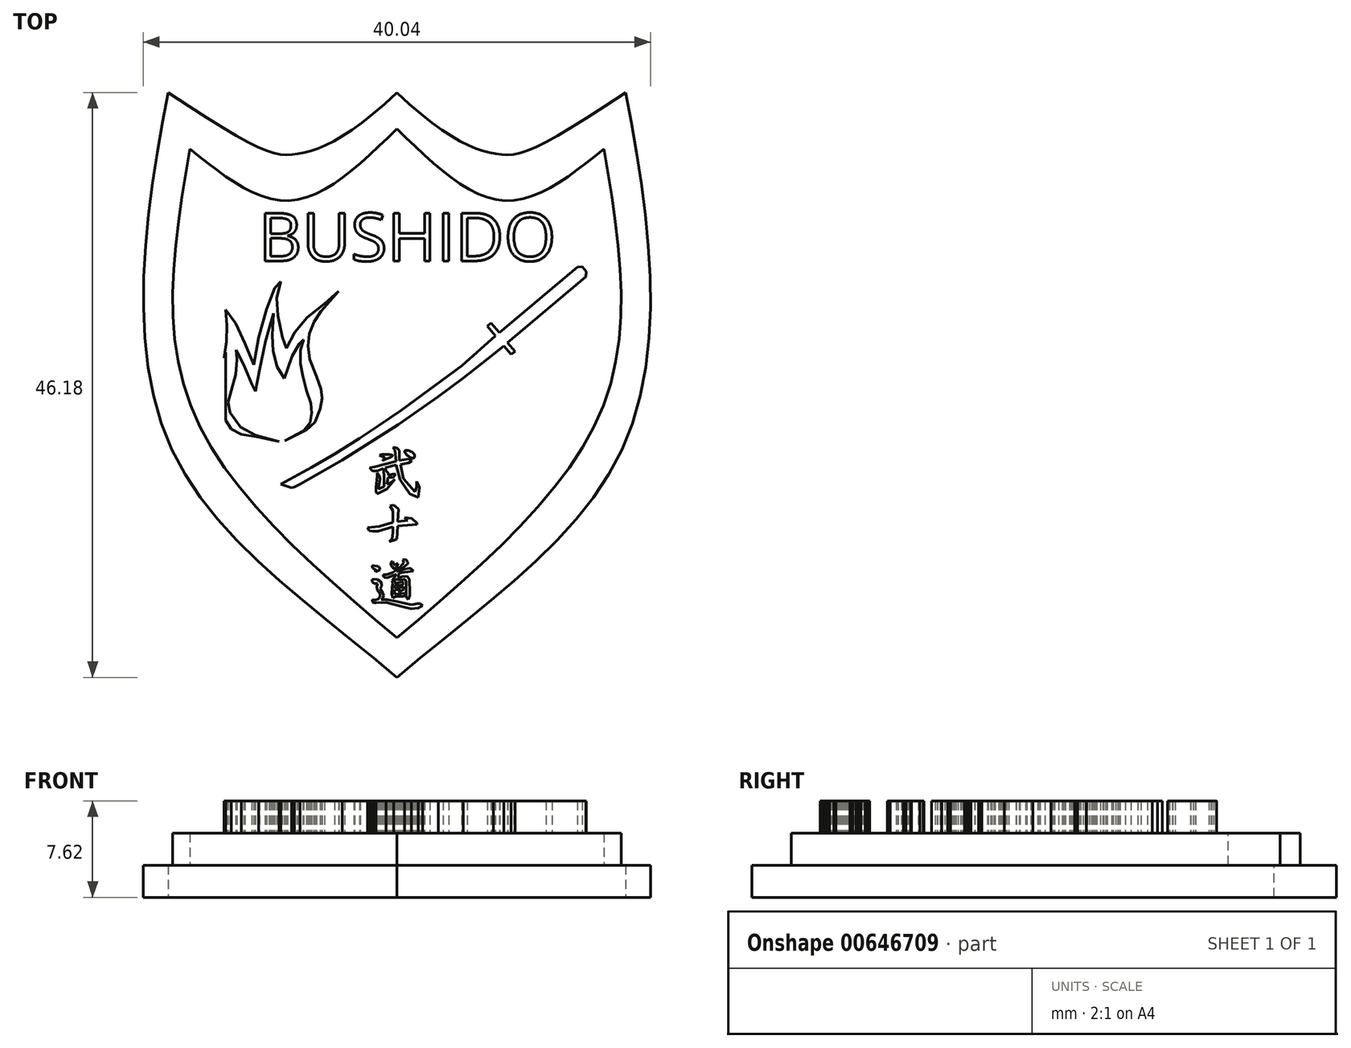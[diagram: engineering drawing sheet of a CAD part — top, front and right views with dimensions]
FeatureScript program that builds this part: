
annotation { "Feature Type Name" : "Feature", "Feature Type Description" : "" }
export const myFeature = defineFeature(function(context is Context, id is Id, definition is map)
    precondition{}
    {
        {
            var Q0;
            Q0=qCreatedBy(makeId("Top.planeOp"),FACE);
            var sketch = newSketch(context, id + "F0", { "sketchPlane" : qUnion([Q0])});
            skFitSpline(sketch, "E0", {"points": [v(0, 0) * mm, v(7.74, -4.83) * mm, v(18.08, 0) * mm], "startDerivative": vector(23.6, -22.28) * mm, "endDerivative": vector(40.6, 26.6) * mm});
            skFitSpline(sketch, "E1", {"points": [v(18.08, 0) * mm, v(18.08, -27.51) * mm, v(0, -46.18) * mm], "startDerivative": vector(10.3, -52.7) * mm, "endDerivative": vector(-42.25, -36.18) * mm});
            skFitSpline(sketch, "E2.MirrorCS", {"points": [v(0, 0) * mm, v(-7.74, -4.83) * mm, v(-18.08, 0) * mm], "startDerivative": vector(-23.6, -22.28) * mm, "endDerivative": vector(-40.6, 26.6) * mm});
            skFitSpline(sketch, "E3.MirrorCS", {"points": [v(-18.08, 0) * mm, v(-18.08, -27.51) * mm, v(0, -46.18) * mm], "startDerivative": vector(-10.3, -52.7) * mm, "endDerivative": vector(42.25, -36.18) * mm});
            skSolve(sketch);
        }
        {
            var Q0;
            Q0=makeQuery(id+"F0.imprint","IMPRINT",FACE,{"disambiguationData":[TD([[makeQuery(id+"F0.imprint","IMPRINT",EDGE,{"derivedFrom":sQuery(id+"F0.wireOp",EDGE,"E0")}),-1.0]])]});
            extrude(context, id + "F1", {"entities" : qUnion([Q0]), "depth" : 2.54 * mm, "offsetDistance" : 25.4 * mm});
        }
        {
            var Q0;
            Q0=qCreatedBy(makeId("Top.planeOp"),FACE);
            var sketch = newSketch(context, id + "F2", { "sketchPlane" : qUnion([Q0])});
            skFitSpline(sketch, "E4", {"points": [v(0, -2.86) * mm, v(8.47, -8.53) * mm, v(16.36, -4.44) * mm], "startDerivative": vector(16.38, -16) * mm, "endDerivative": vector(16.34, 13.17) * mm});
            skFitSpline(sketch, "E5", {"points": [v(16.36, -4.44) * mm, v(16.36, -24.54) * mm, v(0, -43.06) * mm], "startDerivative": vector(7.38, -44.1) * mm, "endDerivative": vector(-39.3, -33.35) * mm});
            skFitSpline(sketch, "E6.MirrorCS", {"points": [v(0, -2.86) * mm, v(-8.47, -8.53) * mm, v(-16.36, -4.44) * mm], "startDerivative": vector(-16.38, -16) * mm, "endDerivative": vector(-16.34, 13.17) * mm});
            skFitSpline(sketch, "E7.MirrorCS", {"points": [v(-16.36, -4.44) * mm, v(-16.36, -24.54) * mm, v(0, -43.06) * mm], "startDerivative": vector(-7.38, -44.1) * mm, "endDerivative": vector(39.3, -33.35) * mm});
            skSolve(sketch);
        }
        {
            var Q0;
            Q0 = qSketchRegion(id + "F2", true);
            extrude(context, id + "F3", {"entities" : qUnion([Q0]), "operationType" : NewBodyOperationType.ADD, "depth" : 5.08 * mm, "offsetDistance" : 25.4 * mm});
        }
        {
            var Q0;
            Q0=makeQuery(id+"F3.opExtrude","CAP_FACE",FACE,{"disambiguationData":[OSD([sQuery(id+"F2.wireOp",EDGE,"E4"),sQuery(id+"F2.wireOp",EDGE,"E5"),sQuery(id+"F2.wireOp",EDGE,"E6.MirrorCS"),sQuery(id+"F2.wireOp",EDGE,"E7.MirrorCS")])],"isStart":false});
            var sketch = newSketch(context, id + "F4", { "sketchPlane" : qUnion([Q0])});
            skText(sketch, "E8", { "text": "BUSHIDO", "fontName": "OpenSans-Regular.ttf"});
            const initialGuessF4  = {"E8": [-0.01092, -0.01329, 1, 0, 0.0038]};
            skSetInitialGuess(sketch, initialGuessF4);
            skSolve(sketch);
        }
        {
            var Q0;
            Q0=makeQuery(id+"F4.imprint","IMPRINT",FACE,{"disambiguationData":[TD([[makeQuery(id+"F4.imprint","IMPRINT",EDGE,{"derivedFrom":sQuery(id+"F4.wireOp",EDGE,"E8.sketch_text.stroke-0")}),1.0]])]});
            var sketch = newSketch(context, id + "F5", { "sketchPlane" : qUnion([Q0])});
            skLineSegment(sketch, "E9", {"start": v(8.08, -18.97) * mm, "end": v(14.27, -13.77) * mm});
            skLineSegment(sketch, "E10", {"start": v(14.27, -13.77) * mm, "end": v(14.65, -13.76) * mm});
            skLineSegment(sketch, "E11", {"start": v(14.65, -13.76) * mm, "end": v(14.97, -14.14) * mm});
            skLineSegment(sketch, "E12", {"start": v(14.97, -14.14) * mm, "end": v(14.92, -14.55) * mm});
            skLineSegment(sketch, "E13", {"start": v(14.92, -14.55) * mm, "end": v(8.74, -19.75) * mm});
            skLineSegment(sketch, "E14", {"start": v(7.14, -18.44) * mm, "end": v(7.43, -18.19) * mm});
            skLineSegment(sketch, "E15", {"start": v(7.43, -18.19) * mm, "end": v(9.32, -20.45) * mm});
            skLineSegment(sketch, "E16", {"start": v(9.32, -20.45) * mm, "end": v(9.02, -20.68) * mm});
            skLineSegment(sketch, "E17", {"start": v(9.02, -20.68) * mm, "end": v(7.14, -18.44) * mm});
            skLineSegment(sketch, "E18", {"start": v(8.53, -19) * mm, "end": v(8.48, -19.24) * mm});
            skLineSegment(sketch, "E19", {"start": v(8.48, -19.24) * mm, "end": v(8.81, -19.3) * mm});
            skLineSegment(sketch, "E20", {"start": v(8.81, -19.3) * mm, "end": v(8.85, -19.08) * mm});
            skLineSegment(sketch, "E21", {"start": v(8.85, -19.08) * mm, "end": v(8.53, -19) * mm});
            skLineSegment(sketch, "E22", {"start": v(8.9, -18.68) * mm, "end": v(8.9, -18.96) * mm});
            skLineSegment(sketch, "E23", {"start": v(8.9, -18.96) * mm, "end": v(9.22, -18.97) * mm});
            skLineSegment(sketch, "E24", {"start": v(9.22, -18.97) * mm, "end": v(9.23, -18.76) * mm});
            skLineSegment(sketch, "E25", {"start": v(9.23, -18.76) * mm, "end": v(8.9, -18.68) * mm});
            skLineSegment(sketch, "E26", {"start": v(9.29, -18.35) * mm, "end": v(9.3, -18.68) * mm});
            skLineSegment(sketch, "E27", {"start": v(9.3, -18.68) * mm, "end": v(9.6, -18.67) * mm});
            skLineSegment(sketch, "E28", {"start": v(9.6, -18.67) * mm, "end": v(9.6, -18.42) * mm});
            skLineSegment(sketch, "E29", {"start": v(9.6, -18.42) * mm, "end": v(9.29, -18.35) * mm});
            skLineSegment(sketch, "E30", {"start": v(9.65, -18.05) * mm, "end": v(9.68, -18.32) * mm});
            skLineSegment(sketch, "E31", {"start": v(9.68, -18.32) * mm, "end": v(9.92, -18.4) * mm});
            skLineSegment(sketch, "E32", {"start": v(9.92, -18.4) * mm, "end": v(9.91, -18.14) * mm});
            skLineSegment(sketch, "E33", {"start": v(9.91, -18.14) * mm, "end": v(9.65, -18.05) * mm});
            skLineSegment(sketch, "E34", {"start": v(10.02, -17.74) * mm, "end": v(10.01, -18) * mm});
            skLineSegment(sketch, "E35", {"start": v(10.01, -18) * mm, "end": v(10.3, -18.09) * mm});
            skLineSegment(sketch, "E36", {"start": v(10.3, -18.09) * mm, "end": v(10.37, -17.86) * mm});
            skLineSegment(sketch, "E37", {"start": v(10.37, -17.86) * mm, "end": v(10.02, -17.74) * mm});
            skLineSegment(sketch, "E38", {"start": v(10.4, -17.43) * mm, "end": v(10.36, -17.7) * mm});
            skLineSegment(sketch, "E39", {"start": v(10.36, -17.7) * mm, "end": v(10.69, -17.73) * mm});
            skLineSegment(sketch, "E40", {"start": v(10.69, -17.73) * mm, "end": v(10.72, -17.52) * mm});
            skLineSegment(sketch, "E41", {"start": v(10.72, -17.52) * mm, "end": v(10.4, -17.43) * mm});
            skLineSegment(sketch, "E42", {"start": v(10.76, -17.12) * mm, "end": v(10.72, -17.36) * mm});
            skLineSegment(sketch, "E43", {"start": v(10.72, -17.36) * mm, "end": v(11.02, -17.4) * mm});
            skLineSegment(sketch, "E44", {"start": v(11.02, -17.4) * mm, "end": v(11.05, -17.22) * mm});
            skLineSegment(sketch, "E45", {"start": v(11.05, -17.22) * mm, "end": v(10.76, -17.12) * mm});
            skLineSegment(sketch, "E46", {"start": v(11.16, -16.79) * mm, "end": v(11.13, -17.06) * mm});
            skLineSegment(sketch, "E47", {"start": v(11.13, -17.06) * mm, "end": v(11.4, -17.08) * mm});
            skLineSegment(sketch, "E48", {"start": v(11.4, -17.08) * mm, "end": v(11.44, -16.9) * mm});
            skLineSegment(sketch, "E49", {"start": v(11.44, -16.9) * mm, "end": v(11.16, -16.79) * mm});
            skLineSegment(sketch, "E50", {"start": v(11.53, -16.45) * mm, "end": v(11.5, -16.7) * mm});
            skLineSegment(sketch, "E51", {"start": v(11.5, -16.7) * mm, "end": v(11.8, -16.76) * mm});
            skLineSegment(sketch, "E52", {"start": v(11.8, -16.76) * mm, "end": v(11.83, -16.54) * mm});
            skLineSegment(sketch, "E53", {"start": v(11.83, -16.54) * mm, "end": v(11.53, -16.45) * mm});
            skLineSegment(sketch, "E54", {"start": v(11.94, -16.13) * mm, "end": v(11.88, -16.4) * mm});
            skLineSegment(sketch, "E55", {"start": v(11.88, -16.4) * mm, "end": v(12.13, -16.46) * mm});
            skLineSegment(sketch, "E56", {"start": v(12.13, -16.46) * mm, "end": v(12.18, -16.24) * mm});
            skLineSegment(sketch, "E57", {"start": v(12.18, -16.24) * mm, "end": v(11.94, -16.13) * mm});
            skLineSegment(sketch, "E58", {"start": v(12.29, -15.84) * mm, "end": v(12.24, -16.12) * mm});
            skLineSegment(sketch, "E59", {"start": v(12.24, -16.12) * mm, "end": v(12.5, -16.23) * mm});
            skLineSegment(sketch, "E60", {"start": v(12.5, -16.23) * mm, "end": v(12.6, -15.97) * mm});
            skLineSegment(sketch, "E61", {"start": v(12.6, -15.97) * mm, "end": v(12.29, -15.84) * mm});
            skLineSegment(sketch, "E62", {"start": v(12.65, -15.53) * mm, "end": v(12.58, -15.82) * mm});
            skLineSegment(sketch, "E63", {"start": v(12.58, -15.82) * mm, "end": v(12.85, -15.88) * mm});
            skLineSegment(sketch, "E64", {"start": v(12.85, -15.88) * mm, "end": v(12.9, -15.63) * mm});
            skLineSegment(sketch, "E65", {"start": v(12.9, -15.63) * mm, "end": v(12.65, -15.53) * mm});
            skLineSegment(sketch, "E66", {"start": v(13.04, -15.2) * mm, "end": v(12.99, -15.5) * mm});
            skLineSegment(sketch, "E67", {"start": v(12.99, -15.5) * mm, "end": v(13.28, -15.55) * mm});
            skLineSegment(sketch, "E68", {"start": v(13.28, -15.55) * mm, "end": v(13.33, -15.3) * mm});
            skLineSegment(sketch, "E69", {"start": v(13.33, -15.3) * mm, "end": v(13.04, -15.2) * mm});
            skLineSegment(sketch, "E70", {"start": v(13.43, -14.88) * mm, "end": v(13.33, -15.13) * mm});
            skLineSegment(sketch, "E71", {"start": v(13.33, -15.13) * mm, "end": v(13.6, -15.23) * mm});
            skLineSegment(sketch, "E72", {"start": v(13.6, -15.23) * mm, "end": v(13.68, -15.02) * mm});
            skLineSegment(sketch, "E73", {"start": v(13.68, -15.02) * mm, "end": v(13.43, -14.88) * mm});
            skLineSegment(sketch, "E74", {"start": v(13.79, -14.58) * mm, "end": v(13.7, -14.83) * mm});
            skLineSegment(sketch, "E75", {"start": v(13.7, -14.83) * mm, "end": v(13.96, -14.94) * mm});
            skLineSegment(sketch, "E76", {"start": v(13.96, -14.94) * mm, "end": v(14.05, -14.71) * mm});
            skLineSegment(sketch, "E77", {"start": v(14.05, -14.71) * mm, "end": v(13.79, -14.58) * mm});
            skPoint(sketch, "E78.orphan", {"position": v(13.8, -14.57) * mm});
            skLineSegment(sketch, "E79", {"start": v(14.13, -14.25) * mm, "end": v(14.09, -14.5) * mm});
            skPoint(sketch, "E79.endSnap0", {"position": v(13.55, -14.95) * mm});
            skLineSegment(sketch, "E80", {"start": v(14.09, -14.5) * mm, "end": v(14.38, -14.64) * mm});
            skLineSegment(sketch, "E81", {"start": v(14.38, -14.64) * mm, "end": v(14.43, -14.35) * mm});
            skLineSegment(sketch, "E82", {"start": v(14.43, -14.35) * mm, "end": v(14.13, -14.25) * mm});
            skLineSegment(sketch, "E83", {"start": v(7.79, -19.21) * mm, "end": v(7.5, -19.97) * mm});
            skLineSegment(sketch, "E84", {"start": v(7.5, -19.97) * mm, "end": v(8.44, -20) * mm});
            skLineSegment(sketch, "E85", {"start": v(8.44, -20) * mm, "end": v(7.62, -20.68) * mm});
            skLineSegment(sketch, "E86", {"start": v(7.62, -20.68) * mm, "end": v(5.23, -22.54) * mm});
            skLineSegment(sketch, "E87", {"start": v(5.23, -22.54) * mm, "end": v(3.27, -23.99) * mm});
            skLineSegment(sketch, "E88", {"start": v(3.27, -23.99) * mm, "end": v(0.1, -26.23) * mm});
            skLineSegment(sketch, "E89", {"start": v(0.1, -26.23) * mm, "end": v(-4.31, -29.03) * mm});
            skLineSegment(sketch, "E90", {"start": v(-4.31, -29.03) * mm, "end": v(-7.65, -30.91) * mm});
            skLineSegment(sketch, "E91", {"start": v(-7.65, -30.91) * mm, "end": v(-8.09, -31.14) * mm});
            skLineSegment(sketch, "E92", {"start": v(-8.09, -31.14) * mm, "end": v(-8.32, -31.2) * mm});
            skLineSegment(sketch, "E93", {"start": v(-8.32, -31.2) * mm, "end": v(-9.18, -30.92) * mm});
            skLineSegment(sketch, "E94", {"start": v(-9.18, -30.92) * mm, "end": v(-6.72, -29.6) * mm});
            skLineSegment(sketch, "E95", {"start": v(-6.72, -29.6) * mm, "end": v(-4.93, -28.55) * mm});
            skLineSegment(sketch, "E96", {"start": v(-4.93, -28.55) * mm, "end": v(-2.96, -27.3) * mm});
            skLineSegment(sketch, "E97", {"start": v(-2.96, -27.3) * mm, "end": v(-1.43, -26.28) * mm});
            skLineSegment(sketch, "E98", {"start": v(-1.43, -26.28) * mm, "end": v(0.36, -25.07) * mm});
            skLineSegment(sketch, "E99", {"start": v(0.36, -25.07) * mm, "end": v(1.86, -23.96) * mm});
            skLineSegment(sketch, "E100", {"start": v(1.86, -23.96) * mm, "end": v(3.69, -22.61) * mm});
            skLineSegment(sketch, "E101", {"start": v(3.69, -22.61) * mm, "end": v(5.14, -21.54) * mm});
            skLineSegment(sketch, "E102", {"start": v(5.14, -21.54) * mm, "end": v(7.79, -19.21) * mm});
            skLineSegment(sketch, "E103", {"start": v(7.5, -19.97) * mm, "end": v(5.5, -21.5) * mm});
            skLineSegment(sketch, "E104", {"start": v(5.5, -21.5) * mm, "end": v(3, -23.43) * mm});
            skLineSegment(sketch, "E105", {"start": v(3, -23.43) * mm, "end": v(1.93, -24.22) * mm});
            skLineSegment(sketch, "E106", {"start": v(1.93, -24.22) * mm, "end": v(0.64, -25.17) * mm});
            skLineSegment(sketch, "E107", {"start": v(0.64, -25.17) * mm, "end": v(-0.46, -25.9) * mm});
            skLineSegment(sketch, "E108", {"start": v(-0.46, -25.9) * mm, "end": v(-1.61, -26.68) * mm});
            skLineSegment(sketch, "E109", {"start": v(-1.61, -26.68) * mm, "end": v(-3.6, -28) * mm});
            skLineSegment(sketch, "E110", {"start": v(-3.6, -28) * mm, "end": v(-5.08, -28.93) * mm});
            skLineSegment(sketch, "E111", {"start": v(-5.08, -28.93) * mm, "end": v(-6.93, -30) * mm});
            skLineSegment(sketch, "E112", {"start": v(-6.93, -30) * mm, "end": v(-8.23, -30.68) * mm});
            skLineSegment(sketch, "E113", {"start": v(-8.23, -30.68) * mm, "end": v(-9.18, -30.92) * mm});
            skLineSegment(sketch, "E114.0", {"start": v(7.79, -19.21) * mm, "end": v(8.08, -18.97) * mm, "construction": true});
            skLineSegment(sketch, "E115.0", {"start": v(8.53, -19) * mm, "end": v(13.8, -14.57) * mm, "construction": true});
            skLineSegment(sketch, "E116.0", {"start": v(13.55, -14.95) * mm, "end": v(14.09, -14.5) * mm, "construction": true});
            skLineSegment(sketch, "E117.0", {"start": v(8.44, -20) * mm, "end": v(8.74, -19.75) * mm, "construction": true});
            skLineSegment(sketch, "E118.0", {"start": v(5.5, -21.5) * mm, "end": v(14.13, -14.25) * mm, "construction": true});
            skLineSegment(sketch, "E119.0", {"start": v(-0.46, -25.9) * mm, "end": v(1.86, -23.96) * mm, "construction": true});
            skLineSegment(sketch, "E120.0", {"start": v(8.08, -18.97) * mm, "end": v(7.43, -18.19) * mm, "construction": true});
            skLineSegment(sketch, "E121.0", {"start": v(9.02, -20.68) * mm, "end": v(7.14, -18.44) * mm, "construction": true});
            skSolve(sketch);
        }
        {
            var Q0;
            Q0=makeQuery(id+"F4.imprint","IMPRINT",FACE,{"disambiguationData":[TD([[makeQuery(id+"F4.imprint","IMPRINT",EDGE,{"derivedFrom":sQuery(id+"F4.wireOp",EDGE,"E8.sketch_text.stroke-0")}),1.0]])]});
            var sketch = newSketch(context, id + "F6", { "sketchPlane" : qUnion([Q0])});
            skFitSpline(sketch, "E122", {"points": [v(-1.36, -28.64) * mm, v(-0.34, -28.66) * mm, v(-1.13, -29.02) * mm, v(-0.95, -28.87) * mm, v(-1.36, -28.64) * mm]});
            skFitSpline(sketch, "E123", {"points": [v(0.6, -28.32) * mm, v(1.28, -28.87) * mm, v(1.3, -28.46) * mm, v(0.6, -28.32) * mm]});
            skLineSegment(sketch, "E124", {"start": v(-0.32, -27.99) * mm, "end": v(0, -28.06) * mm});
            skLineSegment(sketch, "E125", {"start": v(0, -28.06) * mm, "end": v(0.2, -28.26) * mm});
            skLineSegment(sketch, "E126", {"start": v(0.2, -28.26) * mm, "end": v(0.2, -29.06) * mm});
            skLineSegment(sketch, "E127", {"start": v(0.2, -29.06) * mm, "end": v(0.97, -28.92) * mm});
            skLineSegment(sketch, "E128", {"start": v(0.97, -28.92) * mm, "end": v(1.19, -29.1) * mm});
            skLineSegment(sketch, "E129", {"start": v(1.19, -29.1) * mm, "end": v(0.91, -29.24) * mm});
            skLineSegment(sketch, "E130", {"start": v(0.91, -29.24) * mm, "end": v(0.3, -29.36) * mm});
            skLineSegment(sketch, "E131", {"start": v(0.3, -29.36) * mm, "end": v(0.5, -30.49) * mm});
            skLineSegment(sketch, "E132", {"start": v(0.5, -30.49) * mm, "end": v(1.42, -31.54) * mm});
            skLineSegment(sketch, "E133", {"start": v(1.42, -31.54) * mm, "end": v(1.57, -31.13) * mm});
            skLineSegment(sketch, "E134", {"start": v(1.57, -31.13) * mm, "end": v(1.57, -30.7) * mm});
            skLineSegment(sketch, "E135", {"start": v(1.57, -30.7) * mm, "end": v(1.79, -31.19) * mm});
            skLineSegment(sketch, "E136", {"start": v(1.79, -31.19) * mm, "end": v(1.7, -31.96) * mm});
            skLineSegment(sketch, "E137", {"start": v(1.7, -31.96) * mm, "end": v(1.01, -31.69) * mm});
            skLineSegment(sketch, "E138", {"start": v(1.01, -31.69) * mm, "end": v(0.24, -30.58) * mm});
            skLineSegment(sketch, "E139", {"start": v(0.24, -30.58) * mm, "end": v(-0.05, -29.4) * mm});
            skLineSegment(sketch, "E140", {"start": v(-0.05, -29.4) * mm, "end": v(-0.92, -29.62) * mm});
            skLineSegment(sketch, "E141", {"start": v(-0.92, -29.62) * mm, "end": v(-0.85, -29.88) * mm});
            skLineSegment(sketch, "E142", {"start": v(-0.85, -29.88) * mm, "end": v(-0.68, -30.05) * mm});
            skLineSegment(sketch, "E143", {"start": v(-0.68, -30.05) * mm, "end": v(-0.68, -30.21) * mm});
            skLineSegment(sketch, "E144", {"start": v(-0.68, -30.21) * mm, "end": v(-0.36, -30.12) * mm});
            skLineSegment(sketch, "E145", {"start": v(-0.36, -30.12) * mm, "end": v(-0.11, -30.12) * mm});
            skLineSegment(sketch, "E146", {"start": v(-0.11, -30.12) * mm, "end": v(-0.28, -30.4) * mm});
            skLineSegment(sketch, "E147", {"start": v(-0.28, -30.4) * mm, "end": v(-0.7, -30.4) * mm});
            skLineSegment(sketch, "E148", {"start": v(-0.7, -30.4) * mm, "end": v(-0.8, -30.93) * mm});
            skLineSegment(sketch, "E149", {"start": v(-0.8, -30.93) * mm, "end": v(-0.43, -30.76) * mm});
            skLineSegment(sketch, "E150", {"start": v(-0.43, -30.76) * mm, "end": v(-0.16, -30.53) * mm});
            skLineSegment(sketch, "E151", {"start": v(-0.16, -30.53) * mm, "end": v(-0.8, -31.32) * mm});
            skLineSegment(sketch, "E152", {"start": v(-0.8, -31.32) * mm, "end": v(-1.55, -31.69) * mm});
            skLineSegment(sketch, "E153", {"start": v(-1.55, -31.69) * mm, "end": v(-1.65, -31.5) * mm});
            skLineSegment(sketch, "E154", {"start": v(-1.65, -31.5) * mm, "end": v(-1.65, -31.17) * mm});
            skLineSegment(sketch, "E155", {"start": v(-1.65, -31.17) * mm, "end": v(-1.57, -30.28) * mm});
            skLineSegment(sketch, "E156", {"start": v(-1.57, -30.28) * mm, "end": v(-1.57, -30.03) * mm});
            skLineSegment(sketch, "E157", {"start": v(-1.57, -30.03) * mm, "end": v(-1.38, -30.24) * mm});
            skLineSegment(sketch, "E158", {"start": v(-1.38, -30.24) * mm, "end": v(-1.32, -30.5) * mm});
            skLineSegment(sketch, "E159", {"start": v(-1.32, -30.5) * mm, "end": v(-1.46, -31.3) * mm});
            skLineSegment(sketch, "E160", {"start": v(-1.46, -31.3) * mm, "end": v(-1, -31.11) * mm});
            skLineSegment(sketch, "E161", {"start": v(-1, -31.11) * mm, "end": v(-1, -30.23) * mm});
            skLineSegment(sketch, "E162", {"start": v(-1, -30.23) * mm, "end": v(-1.08, -29.68) * mm});
            skLineSegment(sketch, "E163", {"start": v(-1.08, -29.68) * mm, "end": v(-1.57, -29.88) * mm});
            skLineSegment(sketch, "E164", {"start": v(-1.57, -29.88) * mm, "end": v(-1.92, -29.88) * mm});
            skLineSegment(sketch, "E165", {"start": v(-1.92, -29.88) * mm, "end": v(-2.14, -29.63) * mm});
            skLineSegment(sketch, "E166", {"start": v(-2.14, -29.63) * mm, "end": v(-1.79, -29.55) * mm});
            skLineSegment(sketch, "E167", {"start": v(-1.79, -29.55) * mm, "end": v(-0.06, -29.1) * mm});
            skLineSegment(sketch, "E168", {"start": v(-0.06, -29.1) * mm, "end": v(-0.16, -28.24) * mm});
            skLineSegment(sketch, "E169", {"start": v(-0.16, -28.24) * mm, "end": v(-0.32, -27.99) * mm});
            skLineSegment(sketch, "E170", {"start": v(-0.53, -32.65) * mm, "end": v(-0.32, -32.58) * mm});
            skLineSegment(sketch, "E171", {"start": v(-0.32, -32.58) * mm, "end": v(-0.16, -32.65) * mm});
            skLineSegment(sketch, "E172", {"start": v(-0.16, -32.65) * mm, "end": v(0.13, -32.9) * mm});
            skLineSegment(sketch, "E173", {"start": v(0.13, -32.9) * mm, "end": v(0.06, -33.9) * mm});
            skLineSegment(sketch, "E174", {"start": v(0.06, -33.9) * mm, "end": v(0.86, -33.78) * mm});
            skLineSegment(sketch, "E175", {"start": v(0.86, -33.78) * mm, "end": v(0.77, -33.74) * mm});
            skLineSegment(sketch, "E176", {"start": v(0.77, -33.74) * mm, "end": v(0.6, -33.55) * mm});
            skLineSegment(sketch, "E177", {"start": v(0.6, -33.55) * mm, "end": v(1.17, -33.62) * mm});
            skLineSegment(sketch, "E178", {"start": v(1.17, -33.62) * mm, "end": v(1.6, -34) * mm});
            skLineSegment(sketch, "E179", {"start": v(1.6, -34) * mm, "end": v(1.6, -34.11) * mm});
            skLineSegment(sketch, "E180", {"start": v(1.6, -34.11) * mm, "end": v(0.07, -34.21) * mm});
            skLineSegment(sketch, "E181", {"start": v(0.07, -34.21) * mm, "end": v(0, -35.23) * mm});
            skLineSegment(sketch, "E182", {"start": v(0, -35.23) * mm, "end": v(-0.2, -35.34) * mm});
            skLineSegment(sketch, "E183", {"start": v(-0.2, -35.34) * mm, "end": v(-0.6, -35.46) * mm});
            skLineSegment(sketch, "E184", {"start": v(-0.6, -35.46) * mm, "end": v(-0.4, -35.24) * mm});
            skLineSegment(sketch, "E185", {"start": v(-0.4, -35.24) * mm, "end": v(-0.33, -34.77) * mm});
            skLineSegment(sketch, "E186", {"start": v(-0.33, -34.77) * mm, "end": v(-0.33, -34.28) * mm});
            skLineSegment(sketch, "E187", {"start": v(-0.33, -34.28) * mm, "end": v(-1.5, -34.65) * mm});
            skLineSegment(sketch, "E188", {"start": v(-1.5, -34.65) * mm, "end": v(-1.91, -34.65) * mm});
            skLineSegment(sketch, "E189", {"start": v(-1.91, -34.65) * mm, "end": v(-2.2, -34.61) * mm});
            skLineSegment(sketch, "E190", {"start": v(-2.2, -34.61) * mm, "end": v(-2.32, -34.37) * mm});
            skLineSegment(sketch, "E191", {"start": v(-2.32, -34.37) * mm, "end": v(-1.4, -34.27) * mm});
            skLineSegment(sketch, "E192", {"start": v(-1.4, -34.27) * mm, "end": v(-0.32, -33.94) * mm});
            skLineSegment(sketch, "E193", {"start": v(-0.32, -33.94) * mm, "end": v(-0.32, -33) * mm});
            skLineSegment(sketch, "E194", {"start": v(-0.32, -33) * mm, "end": v(-0.53, -32.65) * mm});
            skLineSegment(sketch, "E195", {"start": v(-1.45, -35.63) * mm, "end": v(-0.37, -35.5) * mm});
            skLineSegment(sketch, "E196", {"start": v(-0.37, -35.5) * mm, "end": v(0.26, -35.4) * mm});
            skLineSegment(sketch, "E197", {"start": v(0.26, -35.4) * mm, "end": v(0.53, -35.33) * mm});
            skLineSegment(sketch, "E198", {"start": v(0.53, -35.33) * mm, "end": v(0.72, -35.34) * mm});
            skLineSegment(sketch, "E199", {"start": v(0.72, -35.34) * mm, "end": v(0.95, -35.44) * mm});
            skLineSegment(sketch, "E200", {"start": v(0.95, -35.44) * mm, "end": v(1.05, -35.68) * mm});
            skLineSegment(sketch, "E201", {"start": v(1.05, -35.68) * mm, "end": v(0.77, -35.68) * mm});
            skLineSegment(sketch, "E202", {"start": v(0.77, -35.68) * mm, "end": v(0.35, -35.68) * mm});
            skLineSegment(sketch, "E203", {"start": v(0.35, -35.68) * mm, "end": v(-0.09, -35.68) * mm});
            skLineSegment(sketch, "E204", {"start": v(-0.09, -35.68) * mm, "end": v(-0.72, -35.83) * mm});
            skLineSegment(sketch, "E205", {"start": v(-0.72, -35.83) * mm, "end": v(-1.12, -35.9) * mm});
            skLineSegment(sketch, "E206", {"start": v(-1.12, -35.9) * mm, "end": v(-1.27, -35.83) * mm});
            skLineSegment(sketch, "E207", {"start": v(-1.27, -35.83) * mm, "end": v(-1.45, -35.64) * mm});
            skLineSegment(sketch, "E208", {"start": v(-1.95, -37.35) * mm, "end": v(-1.55, -37.4) * mm});
            skLineSegment(sketch, "E209", {"start": v(-1.55, -37.4) * mm, "end": v(-1.39, -37.48) * mm});
            skLineSegment(sketch, "E210", {"start": v(-1.39, -37.48) * mm, "end": v(-1.34, -37.69) * mm});
            skLineSegment(sketch, "E211", {"start": v(-1.34, -37.69) * mm, "end": v(-1.7, -37.83) * mm});
            skLineSegment(sketch, "E212", {"start": v(-1.7, -37.83) * mm, "end": v(-1.71, -37.73) * mm});
            skLineSegment(sketch, "E213", {"start": v(-1.71, -37.73) * mm, "end": v(-1.63, -37.71) * mm});
            skLineSegment(sketch, "E214", {"start": v(-1.63, -37.71) * mm, "end": v(-1.91, -37.55) * mm});
            skLineSegment(sketch, "E215", {"start": v(-1.91, -37.55) * mm, "end": v(-1.95, -37.35) * mm});
            skLineSegment(sketch, "E216", {"start": v(-0.32, -37.03) * mm, "end": v(-0.3, -37.15) * mm});
            skLineSegment(sketch, "E217", {"start": v(-0.3, -37.15) * mm, "end": v(-0.16, -37.32) * mm});
            skLineSegment(sketch, "E218", {"start": v(-0.16, -37.32) * mm, "end": v(0.1, -37.16) * mm});
            skLineSegment(sketch, "E219", {"start": v(0.1, -37.16) * mm, "end": v(-0.1, -37.67) * mm});
            skLineSegment(sketch, "E220", {"start": v(-0.1, -37.67) * mm, "end": v(-0.36, -37.5) * mm});
            skLineSegment(sketch, "E221", {"start": v(-0.36, -37.5) * mm, "end": v(-0.47, -37.29) * mm});
            skLineSegment(sketch, "E222", {"start": v(-0.47, -37.29) * mm, "end": v(-0.47, -37.11) * mm});
            skLineSegment(sketch, "E223", {"start": v(-0.47, -37.11) * mm, "end": v(-0.32, -37.03) * mm});
            skLineSegment(sketch, "E224", {"start": v(0.5, -36.87) * mm, "end": v(0.71, -36.9) * mm});
            skLineSegment(sketch, "E225", {"start": v(0.71, -36.9) * mm, "end": v(0.84, -37.1) * mm});
            skLineSegment(sketch, "E226", {"start": v(0.84, -37.1) * mm, "end": v(0.87, -37.21) * mm});
            skLineSegment(sketch, "E227", {"start": v(0.87, -37.21) * mm, "end": v(0.39, -37.59) * mm});
            skLineSegment(sketch, "E228", {"start": v(0.39, -37.59) * mm, "end": v(-0.02, -37.77) * mm});
            skLineSegment(sketch, "E229", {"start": v(-0.02, -37.77) * mm, "end": v(0.16, -37.79) * mm});
            skLineSegment(sketch, "E230", {"start": v(0.16, -37.79) * mm, "end": v(0.65, -37.62) * mm});
            skLineSegment(sketch, "E231", {"start": v(0.65, -37.62) * mm, "end": v(1.01, -37.57) * mm});
            skLineSegment(sketch, "E232", {"start": v(1.01, -37.57) * mm, "end": v(1.15, -37.63) * mm});
            skLineSegment(sketch, "E233", {"start": v(1.15, -37.63) * mm, "end": v(1.31, -37.79) * mm});
            skLineSegment(sketch, "E234", {"start": v(1.31, -37.79) * mm, "end": v(0.16, -37.95) * mm});
            skLineSegment(sketch, "E235", {"start": v(0.16, -37.95) * mm, "end": v(0.13, -38.26) * mm});
            skLineSegment(sketch, "E236", {"start": v(0.13, -38.26) * mm, "end": v(0.09, -38.33) * mm});
            skLineSegment(sketch, "E237", {"start": v(0.09, -38.33) * mm, "end": v(0.41, -38.23) * mm});
            skLineSegment(sketch, "E238", {"start": v(0.41, -38.23) * mm, "end": v(0.78, -38.18) * mm});
            skLineSegment(sketch, "E239", {"start": v(0.78, -38.18) * mm, "end": v(1, -38.4) * mm});
            skLineSegment(sketch, "E240", {"start": v(1, -38.4) * mm, "end": v(1.03, -39.54) * mm});
            skLineSegment(sketch, "E241", {"start": v(1.03, -39.54) * mm, "end": v(1, -39.7) * mm});
            skLineSegment(sketch, "E242", {"start": v(1, -39.7) * mm, "end": v(0.88, -40.03) * mm});
            skLineSegment(sketch, "E243", {"start": v(0.88, -40.03) * mm, "end": v(0.71, -39.83) * mm});
            skLineSegment(sketch, "E244", {"start": v(0.71, -39.83) * mm, "end": v(0.71, -38.88) * mm});
            skLineSegment(sketch, "E245", {"start": v(0.71, -38.88) * mm, "end": v(0.71, -38.64) * mm});
            skLineSegment(sketch, "E246", {"start": v(0.71, -38.64) * mm, "end": v(0.64, -38.42) * mm});
            skLineSegment(sketch, "E247", {"start": v(0.64, -38.42) * mm, "end": v(0.42, -38.48) * mm});
            skLineSegment(sketch, "E248", {"start": v(0.42, -38.48) * mm, "end": v(0.11, -38.44) * mm});
            skLineSegment(sketch, "E249", {"start": v(0.11, -38.44) * mm, "end": v(-0.08, -38.44) * mm});
            skLineSegment(sketch, "E250", {"start": v(-0.08, -38.44) * mm, "end": v(-0.2, -38.52) * mm});
            skLineSegment(sketch, "E251", {"start": v(-0.2, -38.52) * mm, "end": v(-0.15, -38.7) * mm});
            skLineSegment(sketch, "E252", {"start": v(-0.15, -38.7) * mm, "end": v(-0.14, -38.74) * mm});
            skLineSegment(sketch, "E253", {"start": v(-0.14, -38.74) * mm, "end": v(0.12, -38.7) * mm});
            skLineSegment(sketch, "E254", {"start": v(0.12, -38.7) * mm, "end": v(0.33, -38.65) * mm});
            skLineSegment(sketch, "E255", {"start": v(0.33, -38.65) * mm, "end": v(0.46, -38.66) * mm});
            skLineSegment(sketch, "E256", {"start": v(0.46, -38.66) * mm, "end": v(0.54, -38.74) * mm});
            skLineSegment(sketch, "E257", {"start": v(0.54, -38.74) * mm, "end": v(0.44, -38.85) * mm});
            skLineSegment(sketch, "E258", {"start": v(0.44, -38.85) * mm, "end": v(0.19, -38.93) * mm});
            skLineSegment(sketch, "E259", {"start": v(0.19, -38.93) * mm, "end": v(0.06, -39.02) * mm});
            skLineSegment(sketch, "E260", {"start": v(0.06, -39.02) * mm, "end": v(0.03, -39) * mm});
            skLineSegment(sketch, "E261", {"start": v(0.03, -39) * mm, "end": v(0.12, -38.92) * mm});
            skLineSegment(sketch, "E262", {"start": v(0.12, -38.92) * mm, "end": v(0.07, -38.9) * mm});
            skLineSegment(sketch, "E263", {"start": v(0.07, -38.9) * mm, "end": v(-0.17, -38.9) * mm});
            skLineSegment(sketch, "E264", {"start": v(-0.17, -38.9) * mm, "end": v(-0.17, -39.14) * mm});
            skLineSegment(sketch, "E265", {"start": v(-0.17, -39.14) * mm, "end": v(0.03, -39.13) * mm});
            skLineSegment(sketch, "E266", {"start": v(0.03, -39.13) * mm, "end": v(0.34, -39.06) * mm});
            skLineSegment(sketch, "E267", {"start": v(0.34, -39.06) * mm, "end": v(0.5, -39.06) * mm});
            skLineSegment(sketch, "E268", {"start": v(0.5, -39.06) * mm, "end": v(0.6, -39.13) * mm});
            skLineSegment(sketch, "E269", {"start": v(0.6, -39.13) * mm, "end": v(0.55, -39.23) * mm});
            skLineSegment(sketch, "E270", {"start": v(0.55, -39.23) * mm, "end": v(0.31, -39.35) * mm});
            skLineSegment(sketch, "E271", {"start": v(0.31, -39.35) * mm, "end": v(0.15, -39.46) * mm});
            skLineSegment(sketch, "E272", {"start": v(0.15, -39.46) * mm, "end": v(0.13, -39.44) * mm});
            skLineSegment(sketch, "E273", {"start": v(0.13, -39.44) * mm, "end": v(0.27, -39.3) * mm});
            skLineSegment(sketch, "E274", {"start": v(0.27, -39.3) * mm, "end": v(-0.15, -39.26) * mm});
            skLineSegment(sketch, "E275", {"start": v(-0.15, -39.26) * mm, "end": v(-0.18, -39.34) * mm});
            skLineSegment(sketch, "E276", {"start": v(-0.18, -39.34) * mm, "end": v(-0.2, -39.62) * mm});
            skLineSegment(sketch, "E277", {"start": v(-0.2, -39.62) * mm, "end": v(-0.06, -39.56) * mm});
            skLineSegment(sketch, "E278", {"start": v(-0.06, -39.56) * mm, "end": v(-0.07, -39.6) * mm});
            skLineSegment(sketch, "E279", {"start": v(-0.07, -39.6) * mm, "end": v(0.11, -39.61) * mm});
            skLineSegment(sketch, "E280", {"start": v(0.11, -39.61) * mm, "end": v(0.42, -39.54) * mm});
            skLineSegment(sketch, "E281", {"start": v(0.42, -39.54) * mm, "end": v(0.59, -39.57) * mm});
            skLineSegment(sketch, "E282", {"start": v(0.59, -39.57) * mm, "end": v(0.66, -39.7) * mm});
            skLineSegment(sketch, "E283", {"start": v(0.66, -39.7) * mm, "end": v(0.63, -39.75) * mm});
            skLineSegment(sketch, "E284", {"start": v(0.63, -39.75) * mm, "end": v(0.46, -39.79) * mm});
            skLineSegment(sketch, "E285", {"start": v(0.46, -39.79) * mm, "end": v(0.12, -39.79) * mm});
            skLineSegment(sketch, "E286", {"start": v(0.12, -39.79) * mm, "end": v(-0.14, -39.82) * mm});
            skLineSegment(sketch, "E287", {"start": v(-0.14, -39.82) * mm, "end": v(-0.3, -39.91) * mm});
            skLineSegment(sketch, "E288", {"start": v(-0.3, -39.91) * mm, "end": v(-0.42, -39.58) * mm});
            skLineSegment(sketch, "E289", {"start": v(-0.42, -39.58) * mm, "end": v(-0.37, -39.08) * mm});
            skLineSegment(sketch, "E290", {"start": v(-0.37, -39.08) * mm, "end": v(-0.33, -38.72) * mm});
            skLineSegment(sketch, "E291", {"start": v(-0.33, -38.72) * mm, "end": v(-0.4, -38.54) * mm});
            skLineSegment(sketch, "E292", {"start": v(-0.4, -38.54) * mm, "end": v(-0.02, -38.03) * mm});
            skLineSegment(sketch, "E293", {"start": v(-0.02, -38.03) * mm, "end": v(-0.78, -38.32) * mm});
            skLineSegment(sketch, "E294", {"start": v(-0.78, -38.32) * mm, "end": v(-0.97, -38.3) * mm});
            skLineSegment(sketch, "E295", {"start": v(-0.97, -38.3) * mm, "end": v(-1.07, -38.19) * mm});
            skLineSegment(sketch, "E296", {"start": v(-1.07, -38.19) * mm, "end": v(-1.09, -38.06) * mm});
            skLineSegment(sketch, "E297", {"start": v(-1.09, -38.06) * mm, "end": v(-0.83, -38.06) * mm});
            skLineSegment(sketch, "E298", {"start": v(-0.83, -38.06) * mm, "end": v(-0.36, -37.92) * mm});
            skLineSegment(sketch, "E299", {"start": v(-0.36, -37.92) * mm, "end": v(0.12, -37.58) * mm});
            skLineSegment(sketch, "E300", {"start": v(0.12, -37.58) * mm, "end": v(0.53, -37.15) * mm});
            skLineSegment(sketch, "E301", {"start": v(0.53, -37.15) * mm, "end": v(0.5, -37) * mm});
            skLineSegment(sketch, "E302", {"start": v(0.5, -37) * mm, "end": v(0.48, -36.9) * mm});
            skLineSegment(sketch, "E303", {"start": v(0.48, -36.9) * mm, "end": v(0.5, -36.87) * mm});
            skLineSegment(sketch, "E304", {"start": v(0.5, -36.87) * mm, "end": v(0.5, -36.87) * mm});
            skLineSegment(sketch, "E305", {"start": v(-1.98, -38.45) * mm, "end": v(-1.77, -38.43) * mm});
            skLineSegment(sketch, "E306", {"start": v(-1.77, -38.43) * mm, "end": v(-1.54, -38.46) * mm});
            skLineSegment(sketch, "E307", {"start": v(-1.54, -38.46) * mm, "end": v(-1.3, -38.6) * mm});
            skLineSegment(sketch, "E308", {"start": v(-1.3, -38.6) * mm, "end": v(-1.2, -38.77) * mm});
            skLineSegment(sketch, "E309", {"start": v(-1.2, -38.77) * mm, "end": v(-1.2, -38.97) * mm});
            skLineSegment(sketch, "E310", {"start": v(-1.2, -38.97) * mm, "end": v(-1.32, -39.17) * mm});
            skLineSegment(sketch, "E311", {"start": v(-1.32, -39.17) * mm, "end": v(-1.1, -39.52) * mm});
            skLineSegment(sketch, "E312", {"start": v(-1.1, -39.52) * mm, "end": v(-1.06, -39.72) * mm});
            skLineSegment(sketch, "E313", {"start": v(-1.06, -39.72) * mm, "end": v(-1.1, -39.92) * mm});
            skLineSegment(sketch, "E314", {"start": v(-1.1, -39.92) * mm, "end": v(-1.24, -40.03) * mm});
            skLineSegment(sketch, "E315", {"start": v(-1.24, -40.03) * mm, "end": v(-0.8, -40.03) * mm});
            skLineSegment(sketch, "E316", {"start": v(-0.8, -40.03) * mm, "end": v(-0.12, -40.15) * mm});
            skLineSegment(sketch, "E317", {"start": v(-0.12, -40.15) * mm, "end": v(0.6, -40.33) * mm});
            skLineSegment(sketch, "E318", {"start": v(0.6, -40.33) * mm, "end": v(1.13, -40.44) * mm});
            skLineSegment(sketch, "E319", {"start": v(1.13, -40.44) * mm, "end": v(1.61, -40.35) * mm});
            skLineSegment(sketch, "E320", {"start": v(1.61, -40.35) * mm, "end": v(1.83, -40.35) * mm});
            skLineSegment(sketch, "E321", {"start": v(1.83, -40.35) * mm, "end": v(2.04, -40.5) * mm});
            skLineSegment(sketch, "E322", {"start": v(2.04, -40.5) * mm, "end": v(1.69, -40.69) * mm});
            skLineSegment(sketch, "E323", {"start": v(1.69, -40.69) * mm, "end": v(1.14, -40.76) * mm});
            skLineSegment(sketch, "E324", {"start": v(1.14, -40.76) * mm, "end": v(0.62, -40.64) * mm});
            skLineSegment(sketch, "E325", {"start": v(0.62, -40.64) * mm, "end": v(-0.24, -40.4) * mm});
            skLineSegment(sketch, "E326", {"start": v(-0.24, -40.4) * mm, "end": v(-0.85, -40.27) * mm});
            skLineSegment(sketch, "E327", {"start": v(-0.85, -40.27) * mm, "end": v(-1.64, -40.3) * mm});
            skLineSegment(sketch, "E328", {"start": v(-1.64, -40.3) * mm, "end": v(-1.79, -40.3) * mm});
            skLineSegment(sketch, "E329", {"start": v(-1.79, -40.3) * mm, "end": v(-1.93, -40.2) * mm});
            skLineSegment(sketch, "E330", {"start": v(-1.93, -40.2) * mm, "end": v(-1.93, -40.03) * mm});
            skLineSegment(sketch, "E331", {"start": v(-1.93, -40.03) * mm, "end": v(-1.72, -40.06) * mm});
            skLineSegment(sketch, "E332", {"start": v(-1.72, -40.06) * mm, "end": v(-1.48, -40.02) * mm});
            skLineSegment(sketch, "E333", {"start": v(-1.48, -40.02) * mm, "end": v(-1.33, -39.81) * mm});
            skLineSegment(sketch, "E334", {"start": v(-1.33, -39.81) * mm, "end": v(-1.33, -39.58) * mm});
            skLineSegment(sketch, "E335", {"start": v(-1.33, -39.58) * mm, "end": v(-1.55, -39.26) * mm});
            skLineSegment(sketch, "E336", {"start": v(-1.55, -39.26) * mm, "end": v(-1.6, -38.98) * mm});
            skLineSegment(sketch, "E337", {"start": v(-1.6, -38.98) * mm, "end": v(-1.52, -38.78) * mm});
            skLineSegment(sketch, "E338", {"start": v(-1.52, -38.78) * mm, "end": v(-1.62, -38.76) * mm});
            skLineSegment(sketch, "E339", {"start": v(-1.62, -38.76) * mm, "end": v(-1.8, -38.76) * mm});
            skLineSegment(sketch, "E340", {"start": v(-1.8, -38.76) * mm, "end": v(-1.93, -38.63) * mm});
            skLineSegment(sketch, "E341", {"start": v(-1.93, -38.63) * mm, "end": v(-1.98, -38.51) * mm});
            skLineSegment(sketch, "E342", {"start": v(-1.98, -38.51) * mm, "end": v(-1.98, -38.45) * mm});
            skSolve(sketch);
        }
        {
            var Q0;
            {var subQ1=sQuery(id+"F5.wireOp",EDGE,"E9");Q0=makeQuery(id+"F5.imprint","IMPRINT",FACE,{"disambiguationData":[TD([[makeQuery(id+"F5.imprint","IMPRINT",EDGE,{"derivedFrom":subQ1}),1.0]])]});}
            var sketch = newSketch(context, id + "F7", { "sketchPlane" : qUnion([Q0])});
            skLineSegment(sketch, "E343", {"start": v(-9.16, -14.92) * mm, "end": v(-9.48, -16.23) * mm});
            skLineSegment(sketch, "E344", {"start": v(-9.48, -16.23) * mm, "end": v(-9.39, -17.6) * mm});
            skLineSegment(sketch, "E345", {"start": v(-9.39, -17.6) * mm, "end": v(-9.05, -19.3) * mm});
            skLineSegment(sketch, "E346", {"start": v(-9.05, -19.3) * mm, "end": v(-8.74, -20.2) * mm});
            skLineSegment(sketch, "E347", {"start": v(-8.74, -20.2) * mm, "end": v(-8.07, -18.93) * mm});
            skLineSegment(sketch, "E348", {"start": v(-8.07, -18.93) * mm, "end": v(-7.09, -17.73) * mm});
            skLineSegment(sketch, "E349", {"start": v(-7.09, -17.73) * mm, "end": v(-5.71, -16.68) * mm});
            skLineSegment(sketch, "E350", {"start": v(-5.71, -16.68) * mm, "end": v(-4.6, -15.67) * mm});
            skLineSegment(sketch, "E351", {"start": v(-4.6, -15.67) * mm, "end": v(-6, -17.27) * mm});
            skLineSegment(sketch, "E352", {"start": v(-6, -17.27) * mm, "end": v(-6.55, -18.1) * mm});
            skLineSegment(sketch, "E353", {"start": v(-6.55, -18.1) * mm, "end": v(-6.92, -19.06) * mm});
            skLineSegment(sketch, "E354", {"start": v(-6.92, -19.06) * mm, "end": v(-7.03, -20) * mm});
            skLineSegment(sketch, "E355", {"start": v(-7.03, -20) * mm, "end": v(-6.89, -21.05) * mm});
            skLineSegment(sketch, "E356", {"start": v(-6.89, -21.05) * mm, "end": v(-6.35, -22.4) * mm});
            skLineSegment(sketch, "E357", {"start": v(-6.35, -22.4) * mm, "end": v(-6, -23.4) * mm});
            skLineSegment(sketch, "E358", {"start": v(-6, -23.4) * mm, "end": v(-5.9, -24.14) * mm});
            skLineSegment(sketch, "E359", {"start": v(-5.9, -24.14) * mm, "end": v(-6.06, -24.98) * mm});
            skLineSegment(sketch, "E360", {"start": v(-6.06, -24.98) * mm, "end": v(-6.48, -26.04) * mm});
            skLineSegment(sketch, "E361", {"start": v(-6.48, -26.04) * mm, "end": v(-7.14, -26.64) * mm});
            skLineSegment(sketch, "E362", {"start": v(-7.14, -26.64) * mm, "end": v(-9.08, -27.61) * mm});
            skLineSegment(sketch, "E363", {"start": v(-9.08, -27.61) * mm, "end": v(-10.93, -27.21) * mm});
            skLineSegment(sketch, "E364", {"start": v(-10.93, -27.21) * mm, "end": v(-12.3, -26.97) * mm});
            skLineSegment(sketch, "E365", {"start": v(-12.3, -26.97) * mm, "end": v(-13.08, -26.56) * mm});
            skLineSegment(sketch, "E366", {"start": v(-13.08, -26.56) * mm, "end": v(-13.64, -25.71) * mm});
            skLineSegment(sketch, "E367", {"start": v(-13.53, -26) * mm, "end": v(-13.64, -25.71) * mm});
            skLineSegment(sketch, "E368", {"start": v(-13.53, -26) * mm, "end": v(-13.53, -20.52) * mm});
            skLineSegment(sketch, "E369", {"start": v(-13.66, -20.96) * mm, "end": v(-13.53, -20.52) * mm});
            skLineSegment(sketch, "E370", {"start": v(-13.66, -20.96) * mm, "end": v(-13.45, -19.65) * mm});
            skLineSegment(sketch, "E371", {"start": v(-13.45, -19.65) * mm, "end": v(-13.43, -18.39) * mm});
            skLineSegment(sketch, "E372", {"start": v(-13.43, -18.39) * mm, "end": v(-13.53, -17.14) * mm});
            skLineSegment(sketch, "E373", {"start": v(-13.53, -17.14) * mm, "end": v(-12.74, -18.23) * mm});
            skLineSegment(sketch, "E374", {"start": v(-12.74, -18.23) * mm, "end": v(-11.99, -19.82) * mm});
            skLineSegment(sketch, "E375", {"start": v(-11.99, -19.82) * mm, "end": v(-11.3, -21.49) * mm});
            skLineSegment(sketch, "E376", {"start": v(-11.3, -21.49) * mm, "end": v(-10.91, -19.33) * mm});
            skLineSegment(sketch, "E377", {"start": v(-10.91, -19.33) * mm, "end": v(-10.3, -17.08) * mm});
            skLineSegment(sketch, "E378", {"start": v(-10.3, -17.08) * mm, "end": v(-9.64, -15.43) * mm});
            skLineSegment(sketch, "E379", {"start": v(-9.64, -15.43) * mm, "end": v(-9.16, -14.92) * mm});
            skLineSegment(sketch, "E380", {"start": v(-9.75, -17.43) * mm, "end": v(-9.85, -19.18) * mm});
            skLineSegment(sketch, "E381", {"start": v(-9.85, -19.18) * mm, "end": v(-9.77, -20.42) * mm});
            skLineSegment(sketch, "E382", {"start": v(-9.77, -20.42) * mm, "end": v(-9.45, -21.64) * mm});
            skLineSegment(sketch, "E383", {"start": v(-9.45, -21.64) * mm, "end": v(-8.88, -22.56) * mm});
            skLineSegment(sketch, "E384", {"start": v(-8.88, -22.56) * mm, "end": v(-8.29, -20.83) * mm});
            skLineSegment(sketch, "E385", {"start": v(-8.29, -20.83) * mm, "end": v(-7.72, -19.85) * mm});
            skLineSegment(sketch, "E386", {"start": v(-7.72, -19.85) * mm, "end": v(-7.38, -19.5) * mm});
            skLineSegment(sketch, "E387", {"start": v(-7.38, -19.5) * mm, "end": v(-7.63, -20.36) * mm});
            skLineSegment(sketch, "E388", {"start": v(-7.63, -20.36) * mm, "end": v(-7.63, -21.4) * mm});
            skLineSegment(sketch, "E389", {"start": v(-7.63, -21.4) * mm, "end": v(-7.44, -22.38) * mm});
            skLineSegment(sketch, "E390", {"start": v(-7.44, -22.38) * mm, "end": v(-7.13, -23.5) * mm});
            skLineSegment(sketch, "E391", {"start": v(-7.13, -23.5) * mm, "end": v(-6.8, -24.53) * mm});
            skLineSegment(sketch, "E392", {"start": v(-6.8, -24.53) * mm, "end": v(-6.73, -25.3) * mm});
            skLineSegment(sketch, "E393", {"start": v(-6.73, -25.3) * mm, "end": v(-6.87, -26.08) * mm});
            skLineSegment(sketch, "E394", {"start": v(-6.87, -26.08) * mm, "end": v(-7.38, -26.68) * mm});
            skLineSegment(sketch, "E395", {"start": v(-7.38, -26.68) * mm, "end": v(-9.08, -27.62) * mm});
            skLineSegment(sketch, "E396", {"start": v(-9.08, -27.62) * mm, "end": v(-11.17, -27.06) * mm});
            skLineSegment(sketch, "E397", {"start": v(-11.17, -27.06) * mm, "end": v(-12.34, -26.4) * mm});
            skLineSegment(sketch, "E398", {"start": v(-12.34, -26.4) * mm, "end": v(-13.18, -25.28) * mm});
            skLineSegment(sketch, "E399", {"start": v(-13.18, -25.28) * mm, "end": v(-13.35, -24.44) * mm});
            skLineSegment(sketch, "E400", {"start": v(-13.35, -24.44) * mm, "end": v(-13.09, -23.52) * mm});
            skLineSegment(sketch, "E401", {"start": v(-13.09, -23.52) * mm, "end": v(-12.72, -22.25) * mm});
            skLineSegment(sketch, "E402", {"start": v(-12.72, -22.25) * mm, "end": v(-12.64, -21.1) * mm});
            skLineSegment(sketch, "E403", {"start": v(-12.64, -21.1) * mm, "end": v(-12.7, -20.32) * mm});
            skLineSegment(sketch, "E404", {"start": v(-12.7, -20.32) * mm, "end": v(-12.11, -21.5) * mm});
            skLineSegment(sketch, "E405", {"start": v(-12.11, -21.5) * mm, "end": v(-11.47, -23.03) * mm});
            skLineSegment(sketch, "E406", {"start": v(-11.47, -23.03) * mm, "end": v(-11.18, -23.6) * mm});
            skLineSegment(sketch, "E407", {"start": v(-11.18, -23.6) * mm, "end": v(-10.87, -21.94) * mm});
            skLineSegment(sketch, "E408", {"start": v(-10.87, -21.94) * mm, "end": v(-10.38, -19.65) * mm});
            skLineSegment(sketch, "E409", {"start": v(-10.38, -19.65) * mm, "end": v(-10.1, -18.63) * mm});
            skLineSegment(sketch, "E410", {"start": v(-10.1, -18.63) * mm, "end": v(-9.75, -17.43) * mm});
            skLineSegment(sketch, "E411", {"start": v(-10.03, -21.12) * mm, "end": v(-10.06, -21.55) * mm});
            skLineSegment(sketch, "E412", {"start": v(-10.06, -21.55) * mm, "end": v(-10, -22.16) * mm});
            skLineSegment(sketch, "E413", {"start": v(-10, -22.16) * mm, "end": v(-9.76, -23.11) * mm});
            skLineSegment(sketch, "E414", {"start": v(-9.76, -23.11) * mm, "end": v(-9.05, -24.53) * mm});
            skLineSegment(sketch, "E415", {"start": v(-9.05, -24.53) * mm, "end": v(-8.72, -23.34) * mm});
            skLineSegment(sketch, "E416", {"start": v(-8.72, -23.34) * mm, "end": v(-8.43, -22.77) * mm});
            skLineSegment(sketch, "E417", {"start": v(-8.43, -22.77) * mm, "end": v(-7.98, -22.31) * mm});
            skLineSegment(sketch, "E418", {"start": v(-7.98, -22.31) * mm, "end": v(-8.14, -22.72) * mm});
            skLineSegment(sketch, "E419", {"start": v(-8.14, -22.72) * mm, "end": v(-8.18, -23.27) * mm});
            skLineSegment(sketch, "E420", {"start": v(-8.18, -23.27) * mm, "end": v(-8.04, -23.95) * mm});
            skLineSegment(sketch, "E421", {"start": v(-8.04, -23.95) * mm, "end": v(-7.73, -24.76) * mm});
            skLineSegment(sketch, "E422", {"start": v(-7.73, -24.76) * mm, "end": v(-7.49, -25.39) * mm});
            skLineSegment(sketch, "E423", {"start": v(-7.49, -25.39) * mm, "end": v(-7.33, -25.71) * mm});
            skLineSegment(sketch, "E424", {"start": v(-7.33, -25.71) * mm, "end": v(-7.46, -26.05) * mm});
            skLineSegment(sketch, "E425", {"start": v(-7.46, -26.05) * mm, "end": v(-8.12, -26.96) * mm});
            skLineSegment(sketch, "E426", {"start": v(-8.12, -26.96) * mm, "end": v(-9.08, -27.44) * mm});
            skLineSegment(sketch, "E427", {"start": v(-9.08, -27.44) * mm, "end": v(-11.2, -26.74) * mm});
            skLineSegment(sketch, "E428", {"start": v(-11.2, -26.74) * mm, "end": v(-11.96, -26.21) * mm});
            skLineSegment(sketch, "E429", {"start": v(-11.96, -26.21) * mm, "end": v(-12.37, -25.62) * mm});
            skLineSegment(sketch, "E430", {"start": v(-12.37, -25.62) * mm, "end": v(-12.57, -24.84) * mm});
            skLineSegment(sketch, "E431", {"start": v(-12.57, -24.84) * mm, "end": v(-12.43, -23.97) * mm});
            skLineSegment(sketch, "E432", {"start": v(-12.43, -23.97) * mm, "end": v(-12.25, -23.03) * mm});
            skLineSegment(sketch, "E433", {"start": v(-12.25, -23.03) * mm, "end": v(-12.25, -22.34) * mm});
            skLineSegment(sketch, "E434", {"start": v(-12.25, -22.34) * mm, "end": v(-11.87, -23.1) * mm});
            skLineSegment(sketch, "E435", {"start": v(-11.87, -23.1) * mm, "end": v(-11.4, -23.73) * mm});
            skLineSegment(sketch, "E436", {"start": v(-11.4, -23.73) * mm, "end": v(-10.67, -24.6) * mm});
            skLineSegment(sketch, "E437", {"start": v(-10.67, -24.6) * mm, "end": v(-10.59, -23.32) * mm});
            skLineSegment(sketch, "E438", {"start": v(-10.59, -23.32) * mm, "end": v(-10.43, -22.27) * mm});
            skLineSegment(sketch, "E439", {"start": v(-10.43, -22.27) * mm, "end": v(-10.2, -21.44) * mm});
            skLineSegment(sketch, "E440", {"start": v(-10.2, -21.44) * mm, "end": v(-10.03, -21.12) * mm});
            skLineSegment(sketch, "E441", {"start": v(-8.22, -24.45) * mm, "end": v(-8.25, -24.96) * mm});
            skLineSegment(sketch, "E442", {"start": v(-8.25, -24.96) * mm, "end": v(-8.1, -25.76) * mm});
            skLineSegment(sketch, "E443", {"start": v(-8.1, -25.76) * mm, "end": v(-7.94, -26.35) * mm});
            skLineSegment(sketch, "E444", {"start": v(-7.94, -26.35) * mm, "end": v(-8.03, -26.83) * mm});
            skLineSegment(sketch, "E445", {"start": v(-8.03, -26.83) * mm, "end": v(-9.08, -27.36) * mm});
            skLineSegment(sketch, "E446", {"start": v(-9.08, -27.36) * mm, "end": v(-10.44, -26.88) * mm});
            skLineSegment(sketch, "E447", {"start": v(-10.44, -26.88) * mm, "end": v(-11.26, -26.44) * mm});
            skLineSegment(sketch, "E448", {"start": v(-11.26, -26.44) * mm, "end": v(-11.67, -26.07) * mm});
            skLineSegment(sketch, "E449", {"start": v(-11.67, -26.07) * mm, "end": v(-11.84, -25.73) * mm});
            skLineSegment(sketch, "E450", {"start": v(-11.84, -25.73) * mm, "end": v(-11.9, -25.03) * mm});
            skLineSegment(sketch, "E451", {"start": v(-11.9, -25.03) * mm, "end": v(-11.9, -24.35) * mm});
            skLineSegment(sketch, "E452", {"start": v(-11.9, -24.35) * mm, "end": v(-12.1, -23.79) * mm});
            skLineSegment(sketch, "E453", {"start": v(-12.1, -23.79) * mm, "end": v(-11.56, -24.42) * mm});
            skLineSegment(sketch, "E454", {"start": v(-11.56, -24.42) * mm, "end": v(-10.47, -25.53) * mm});
            skLineSegment(sketch, "E455", {"start": v(-10.47, -25.53) * mm, "end": v(-10.12, -25.79) * mm});
            skLineSegment(sketch, "E456", {"start": v(-10.12, -25.79) * mm, "end": v(-10.07, -24.97) * mm});
            skLineSegment(sketch, "E457", {"start": v(-10.07, -24.97) * mm, "end": v(-9.9, -24.34) * mm});
            skLineSegment(sketch, "E458", {"start": v(-9.9, -24.34) * mm, "end": v(-9.75, -25.1) * mm});
            skLineSegment(sketch, "E459", {"start": v(-9.75, -25.1) * mm, "end": v(-9.47, -25.66) * mm});
            skLineSegment(sketch, "E460", {"start": v(-9.47, -25.66) * mm, "end": v(-9, -26.34) * mm});
            skLineSegment(sketch, "E461", {"start": v(-9, -26.34) * mm, "end": v(-8.92, -25.39) * mm});
            skLineSegment(sketch, "E462", {"start": v(-8.92, -25.39) * mm, "end": v(-8.7, -24.85) * mm});
            skLineSegment(sketch, "E463", {"start": v(-8.7, -24.85) * mm, "end": v(-8.22, -24.45) * mm});
            skSolve(sketch);
        }
        {
            var Q0;
            Q0 = qSketchRegion(id + "F4", true);
            var Q1;
            {var subQ4=sQuery(id+"F5.wireOp",EDGE,"E9");Q1=makeQuery(id+"F7.imprint","IMPRINT",FACE,{"disambiguationData":[TD([[makeQuery(id+"F7.imprint","IMPRINT",EDGE,{"derivedFrom":makeQuery(id+"F5.imprint","IMPRINT",EDGE,{"derivedFrom":subQ4})}),-1.0]])]});}
            extrude(context, id + "F8", {"entities" : qUnion([Q0, Q1]), "operationType" : NewBodyOperationType.ADD, "depth" : 2.54 * mm, "offsetDistance" : 25.4 * mm});
        }
        {
            var Q0;
            Q0=makeQuery(id+"F7.imprint","IMPRINT",FACE,{"disambiguationData":[TD([[makeQuery(id+"F7.imprint","IMPRINT",EDGE,{"derivedFrom":sQuery(id+"F7.wireOp",EDGE,"E343")}),-1.0]])]});
            extrude(context, id + "F9", {"entities" : qUnion([Q0]), "operationType" : NewBodyOperationType.ADD, "depth" : 2.54 * mm, "offsetDistance" : 25.4 * mm});
        }
        {
            var Q0;
            Q0 = qSketchRegion(id + "F6", true);
            extrude(context, id + "F10", {"entities" : qUnion([Q0]), "operationType" : NewBodyOperationType.ADD, "depth" : 2.54 * mm, "offsetDistance" : 25.4 * mm});
        }
    });
